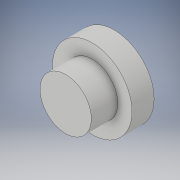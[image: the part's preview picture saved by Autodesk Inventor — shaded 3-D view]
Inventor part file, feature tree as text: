
AUTODESK INVENTOR PART (.ipt)
format: ipt  version: 2019 (Build 230136000, 136)  size: 108,544 bytes
history: native  units: in
note: dims shown in document units (in); Inventor stores cm internally (conversion verified against a paired STEP export)
features: extrude x3, sketch x3
ambient origin geometry x8: Origin, YZ Plane, XZ Plane, XY Plane, X Axis, Y Axis, Z Axis, Center Point
bodies: Solid1 (feature_tree)
feature tree (6):
  extrude  "Extrusion1"  Depth=0.125in TaperAngle=0.0deg
  extrude  "Extrusion2"  Depth=0.05in TaperAngle=0.0deg
  extrude  "Extrusion3"  Depth=0.1in TaperAngle=0.0deg
  sketch  "Sketch1"  dims[d0=0.45in d1=0.125in d2=0.0in]
  sketch  "Sketch2"  dims[d3=0.29in d4=0.05in d5=0.0in]
  sketch  "Sketch3"  dims[d6=0.29in d7=0.1in d8=0.0in]
